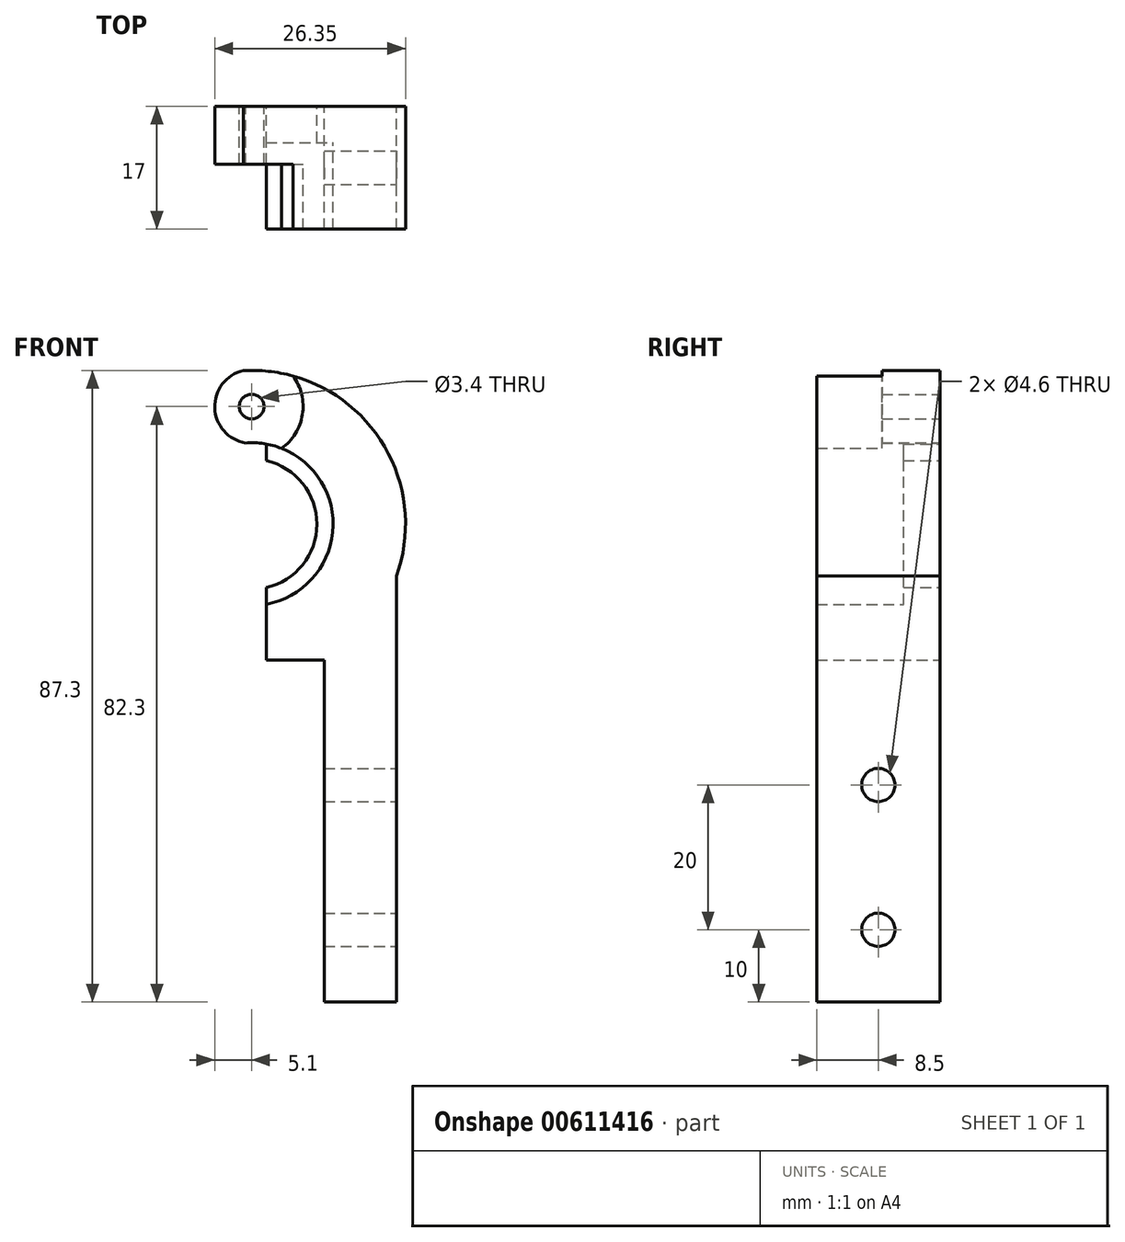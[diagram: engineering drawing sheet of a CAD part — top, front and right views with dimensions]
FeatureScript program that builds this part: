
annotation { "Feature Type Name" : "Feature", "Feature Type Description" : "" }
export const myFeature = defineFeature(function(context is Context, id is Id, definition is map)
    precondition{}
    {
        {
            var Q0;
            Q0=qCreatedBy(makeId("Front.planeOp"),FACE);
            var sketch = newSketch(context, id + "F0", { "sketchPlane" : qUnion([Q0])});
            skCircle(sketch, "E0", {"center": v(0, 0) * mm, "radius": 11.25 * mm});
            skCircle(sketch, "E1.0", {"center": v(0, 0) * mm, "radius": 21.25 * mm});
            skCircle(sketch, "E2", {"center": v(0, 16.25) * mm, "radius": 1.7 * mm});
            skCircle(sketch, "E3.0", {"center": v(0, 16.25) * mm, "radius": 5.1 * mm});
            skCircle(sketch, "E4.0", {"center": v(0, 16.25) * mm, "radius": 7.1 * mm});
            skLineSegment(sketch, "E5", {"start": v(10, -66.05) * mm, "end": v(10, -18.75) * mm});
            skLineSegment(sketch, "E6", {"start": v(10, -66.05) * mm, "end": v(20, -66.05) * mm});
            skLineSegment(sketch, "E7", {"start": v(20, -66.05) * mm, "end": v(20, -7.18) * mm});
            skLineSegment(sketch, "E8", {"start": v(10, -18.75) * mm, "end": v(-10, -18.75) * mm});
            skCircle(sketch, "E9", {"center": v(0, 0) * mm, "radius": 9 * mm});
            skLineSegment(sketch, "E10", {"start": v(2, -18.75) * mm, "end": v(2, -8.77) * mm});
            skLineSegment(sketch, "E11", {"start": v(2, 8.77) * mm, "end": v(2, 11.07) * mm});
            skSolve(sketch);
        }
        {
            var Q0;
            {var subQ0=sQuery(id+"F0.wireOp",EDGE,"E4.0");var subQ3=sQuery(id+"F0.wireOp",EDGE,"E0");var subQ4=makeQuery(id+"F0.imprint","INTERSECT",VERTEX,{"disambiguationData":[OD(0.0)],"derivedFrom":[subQ3,subQ0]});Q0=makeQuery(id+"F0.imprint","IMPRINT",FACE,{"disambiguationData":[TD([[makeQuery(id+"F0.imprint","IMPRINT",EDGE,{"disambiguationData":[TD([[subQ4,1.0]])],"derivedFrom":subQ3}),-1.0]])]});}
            var Q1;
            {var subQ1=sQuery(id+"F0.wireOp",EDGE,"E0");var subQ5=makeQuery(id+"F0.imprint","INTERSECT",VERTEX,{"derivedFrom":[subQ1,sQuery(id+"F0.wireOp",EDGE,"E11")]});Q1=makeQuery(id+"F0.imprint","IMPRINT",FACE,{"disambiguationData":[TD([[makeQuery(id+"F0.imprint","IMPRINT",EDGE,{"disambiguationData":[TD([[subQ5,1.0]])],"derivedFrom":subQ1}),-1.0]])]});}
            var Q2;
            Q2=makeQuery(id+"F0.imprint","IMPRINT",FACE,{"disambiguationData":[TD([[makeQuery(id+"F0.imprint","IMPRINT",EDGE,{"derivedFrom":sQuery(id+"F0.wireOp",EDGE,"E2")}),-1.0]])]});
            var Q3;
            {var subQ5=sQuery(id+"F0.wireOp",EDGE,"E0");var subQ7=sQuery(id+"F0.wireOp",EDGE,"E4.0");var subQ8=makeQuery(id+"F0.imprint","INTERSECT",VERTEX,{"disambiguationData":[OD(0.0)],"derivedFrom":[subQ5,subQ7]});Q3=makeQuery(id+"F0.imprint","IMPRINT",FACE,{"disambiguationData":[TD([[makeQuery(id+"F0.imprint","IMPRINT",EDGE,{"disambiguationData":[TD([[subQ8,1.0]])],"derivedFrom":subQ5}),1.0]])]});}
            var Q4;
            {var subQ0=sQuery(id+"F0.wireOp",EDGE,"E11");var subQ1=sQuery(id+"F0.wireOp",EDGE,"E0");var subQ2=makeQuery(id+"F0.imprint","INTERSECT",VERTEX,{"derivedFrom":[subQ1,subQ0]});Q4=makeQuery(id+"F0.imprint","IMPRINT",FACE,{"disambiguationData":[TD([[makeQuery(id+"F0.imprint","IMPRINT",EDGE,{"disambiguationData":[TD([[subQ2,1.0]])],"derivedFrom":subQ1}),1.0]])]});}
            var Q5;
            {var subQ0=sQuery(id+"F0.wireOp",EDGE,"E5");Q5=makeQuery(id+"F0.imprint","IMPRINT",FACE,{"disambiguationData":[TD([[makeQuery(id+"F0.imprint","IMPRINT",EDGE,{"derivedFrom":subQ0}),-1.0]])]});}
            extrude(context, id + "F1", {"entities" : qUnion([Q0, Q1, Q2, Q3, Q4, Q5]), "depth" : 5 * mm, "offsetDistance" : 25 * mm});
        }
        {
            var Q0;
            {var subQ0=sQuery(id+"F0.wireOp",EDGE,"E4.0");var subQ3=sQuery(id+"F0.wireOp",EDGE,"E0");var subQ4=makeQuery(id+"F0.imprint","INTERSECT",VERTEX,{"disambiguationData":[OD(0.0)],"derivedFrom":[subQ3,subQ0]});Q0=makeQuery(id+"F0.imprint","IMPRINT",FACE,{"disambiguationData":[TD([[makeQuery(id+"F0.imprint","IMPRINT",EDGE,{"disambiguationData":[TD([[subQ4,1.0]])],"derivedFrom":subQ3}),-1.0]])]});}
            var Q1;
            {var subQ1=sQuery(id+"F0.wireOp",EDGE,"E0");var subQ5=makeQuery(id+"F0.imprint","INTERSECT",VERTEX,{"derivedFrom":[subQ1,sQuery(id+"F0.wireOp",EDGE,"E11")]});Q1=makeQuery(id+"F0.imprint","IMPRINT",FACE,{"disambiguationData":[TD([[makeQuery(id+"F0.imprint","IMPRINT",EDGE,{"disambiguationData":[TD([[subQ5,1.0]])],"derivedFrom":subQ1}),-1.0]])]});}
            var Q2;
            Q2=makeQuery(id+"F0.imprint","IMPRINT",FACE,{"disambiguationData":[TD([[makeQuery(id+"F0.imprint","IMPRINT",EDGE,{"derivedFrom":sQuery(id+"F0.wireOp",EDGE,"E2")}),-1.0]])]});
            var Q3;
            {var subQ0=sQuery(id+"F0.wireOp",EDGE,"E5");Q3=makeQuery(id+"F0.imprint","IMPRINT",FACE,{"disambiguationData":[TD([[makeQuery(id+"F0.imprint","IMPRINT",EDGE,{"derivedFrom":subQ0}),-1.0]])]});}
            extrude(context, id + "F2", {"entities" : qUnion([Q0, Q1, Q2, Q3]), "operationType" : NewBodyOperationType.ADD, "depth" : 8 * mm, "offsetDistance" : 25 * mm});
        }
        {
            var Q0;
            {var subQ0=sQuery(id+"F0.wireOp",EDGE,"E5");Q0=makeQuery(id+"F0.imprint","IMPRINT",FACE,{"disambiguationData":[TD([[makeQuery(id+"F0.imprint","IMPRINT",EDGE,{"derivedFrom":subQ0}),-1.0]])]});}
            var Q1;
            {var subQ0=sQuery(id+"F0.wireOp",EDGE,"E4.0");var subQ3=sQuery(id+"F0.wireOp",EDGE,"E0");var subQ4=makeQuery(id+"F0.imprint","INTERSECT",VERTEX,{"disambiguationData":[OD(0.0)],"derivedFrom":[subQ3,subQ0]});Q1=makeQuery(id+"F0.imprint","IMPRINT",FACE,{"disambiguationData":[TD([[makeQuery(id+"F0.imprint","IMPRINT",EDGE,{"disambiguationData":[TD([[subQ4,1.0]])],"derivedFrom":subQ3}),-1.0]])]});}
            extrude(context, id + "F3", {"entities" : qUnion([Q0, Q1]), "operationType" : NewBodyOperationType.ADD, "depth" : 17 * mm, "offsetDistance" : 25 * mm});
        }
        {
            var Q0;
            {var subQ0=sQuery(id+"F0.wireOp",EDGE,"E7");Q0=makeQuery(id+"F3.boolean.opBoolean","MERGE",FACE,{"derivedFrom":[makeQuery(id+"F2.boolean.opBoolean","MERGE",FACE,{"derivedFrom":[makeQuery(id+"F1.opExtrude","SWEPT_FACE",FACE,{"disambiguationData":[OSD([subQ0])]}),makeQuery(id+"F2.opExtrude","SWEPT_FACE",FACE,{"disambiguationData":[OSD([subQ0])]})]}),makeQuery(id+"F3.opExtrude","SWEPT_FACE",FACE,{"disambiguationData":[OSD([subQ0])]})]});}
            var sketch = newSketch(context, id + "F4", { "sketchPlane" : qUnion([Q0])});
            skCircle(sketch, "E12", {"center": v(-8.5, -56.05) * mm, "radius": 2.3 * mm});
            skCircle(sketch, "E13", {"center": v(-8.5, -36.05) * mm, "radius": 2.3 * mm});
            skSolve(sketch);
        }
        {
            var Q0;
            Q0=makeQuery(id+"F4.imprint","IMPRINT",FACE,{"disambiguationData":[TD([[makeQuery(id+"F4.imprint","IMPRINT",EDGE,{"derivedFrom":sQuery(id+"F4.wireOp",EDGE,"E12")}),1.0]])]});
            var Q1;
            Q1=makeQuery(id+"F4.imprint","IMPRINT",FACE,{"disambiguationData":[TD([[makeQuery(id+"F4.imprint","IMPRINT",EDGE,{"derivedFrom":sQuery(id+"F4.wireOp",EDGE,"E13")}),1.0]])]});
            extrude(context, id + "F5", {"entities" : qUnion([Q0, Q1]), "operationType" : NewBodyOperationType.REMOVE, "oppositeDirection" : true, "depth" : 25 * mm, "offsetDistance" : 25 * mm});
        }
    });
